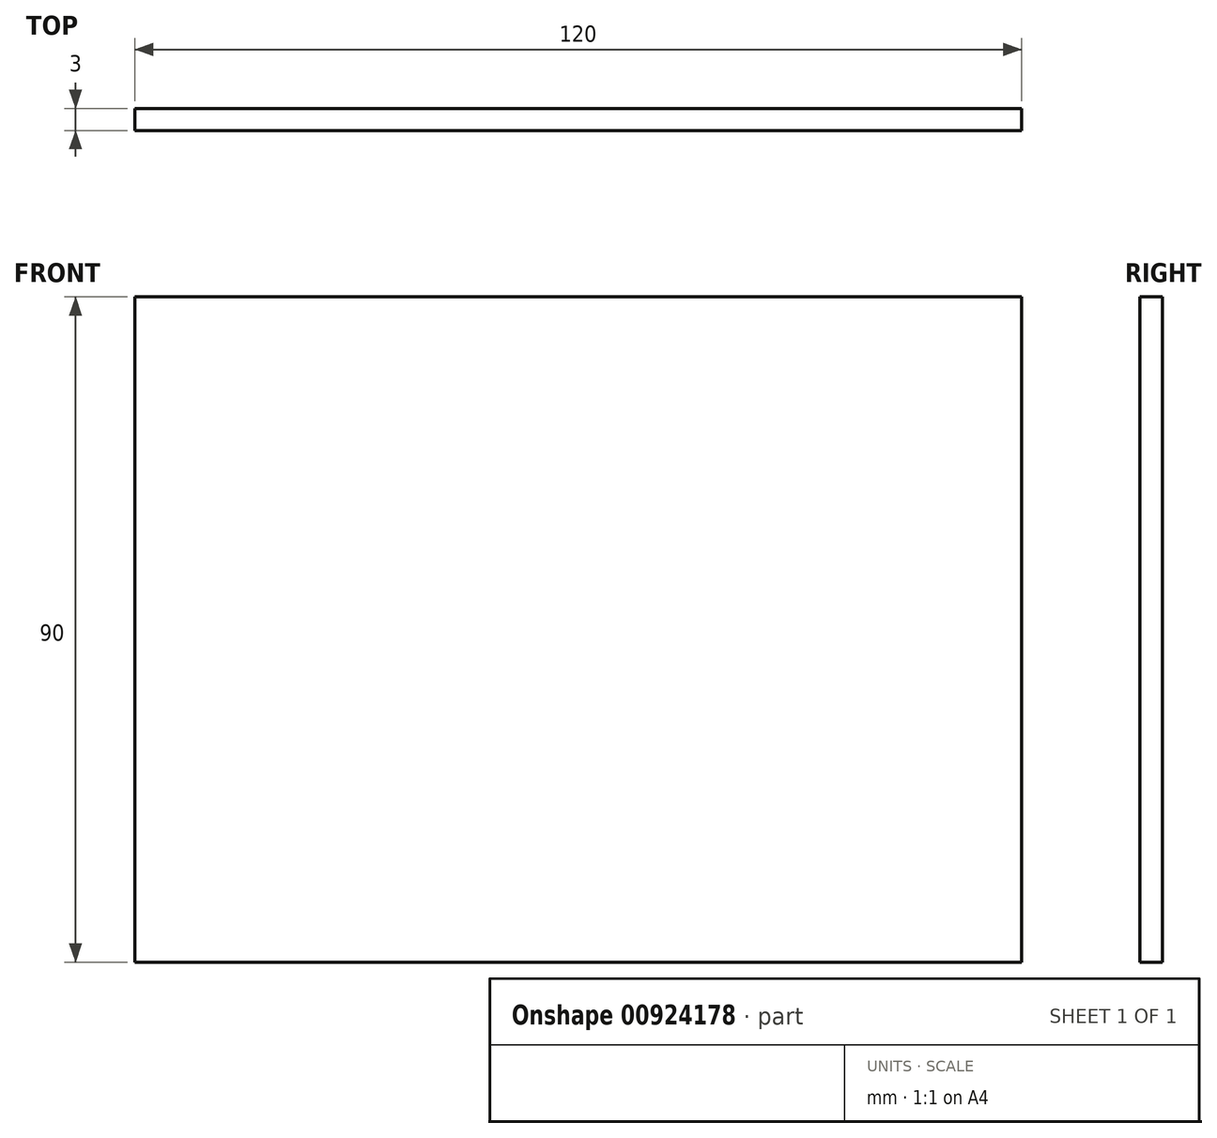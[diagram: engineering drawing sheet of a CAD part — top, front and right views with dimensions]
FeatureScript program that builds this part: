
annotation { "Feature Type Name" : "Feature", "Feature Type Description" : "" }
export const myFeature = defineFeature(function(context is Context, id is Id, definition is map)
    precondition{}
    {
        {
            var Q0;
            Q0=qCreatedBy(makeId("Front.planeOp"),FACE);
            var sketch = newSketch(context, id + "F0", { "sketchPlane" : qUnion([Q0])});
            skLineSegment(sketch, "E0.bottom", {"start": v(-58.5, 55.78) * mm, "end": v(61.5, 55.78) * mm});
            skLineSegment(sketch, "E0.top", {"start": v(-58.5, -34.22) * mm, "end": v(61.5, -34.22) * mm});
            skLineSegment(sketch, "E0.left", {"start": v(-58.5, 55.78) * mm, "end": v(-58.5, -34.22) * mm});
            skLineSegment(sketch, "E0.right", {"start": v(61.5, 55.78) * mm, "end": v(61.5, -34.22) * mm});
            skSolve(sketch);
        }
        {
            var Q0;
            Q0=makeQuery(id+"F0.imprint","IMPRINT",FACE,{"disambiguationData":[TD([[makeQuery(id+"F0.imprint","IMPRINT",EDGE,{"derivedFrom":sQuery(id+"F0.wireOp",EDGE,"E0.bottom")}),-1.0]])]});
            extrude(context, id + "F1", {"entities" : qUnion([Q0]), "depth" : 3 * mm, "offsetDistance" : 25 * mm});
        }
    });
